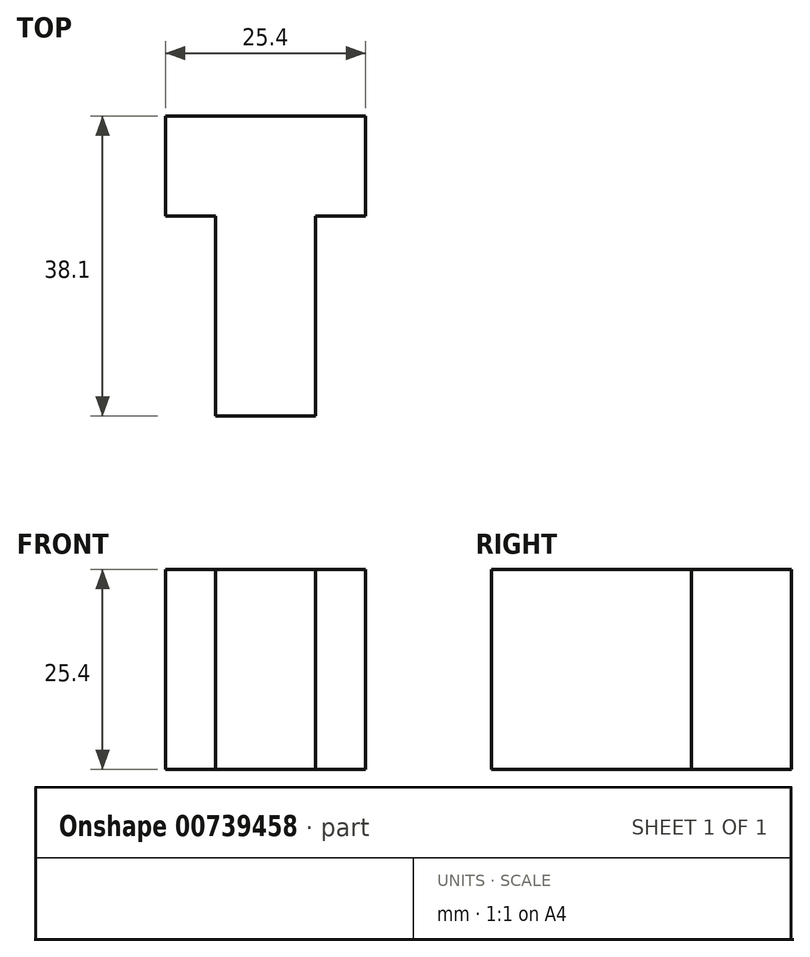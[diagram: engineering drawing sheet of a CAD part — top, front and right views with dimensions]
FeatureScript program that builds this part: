
annotation { "Feature Type Name" : "Feature", "Feature Type Description" : "" }
export const myFeature = defineFeature(function(context is Context, id is Id, definition is map)
    precondition{}
    {
        {
            var Q0;
            Q0=qCreatedBy(makeId("Top.planeOp"),FACE);
            var sketch = newSketch(context, id + "F0", { "sketchPlane" : qUnion([Q0])});
            skLineSegment(sketch, "E0", {"start": v(0, 0) * mm, "end": v(25.4, 0) * mm});
            skLineSegment(sketch, "E1", {"start": v(25.4, 0) * mm, "end": v(25.4, -12.7) * mm});
            skLineSegment(sketch, "E2", {"start": v(25.4, -12.7) * mm, "end": v(19.05, -12.7) * mm});
            skLineSegment(sketch, "E3", {"start": v(19.05, -12.7) * mm, "end": v(19.05, -38.1) * mm});
            skLineSegment(sketch, "E4", {"start": v(19.05, -38.1) * mm, "end": v(6.35, -38.1) * mm});
            skLineSegment(sketch, "E5", {"start": v(6.35, -38.1) * mm, "end": v(6.35, -12.7) * mm});
            skLineSegment(sketch, "E6", {"start": v(6.35, -12.7) * mm, "end": v(0, -12.7) * mm});
            skLineSegment(sketch, "E7", {"start": v(0, -12.7) * mm, "end": v(0, 0) * mm});
            skSolve(sketch);
        }
        {
            var Q0;
            Q0=makeQuery(id+"F0.imprint","IMPRINT",FACE,{"disambiguationData":[TD([[makeQuery(id+"F0.imprint","IMPRINT",EDGE,{"derivedFrom":sQuery(id+"F0.wireOp",EDGE,"E0")}),-1.0]])]});
            extrude(context, id + "F1", {"entities" : qUnion([Q0]), "depth" : 25.4 * mm, "offsetDistance" : 25.4 * mm});
        }
    });
